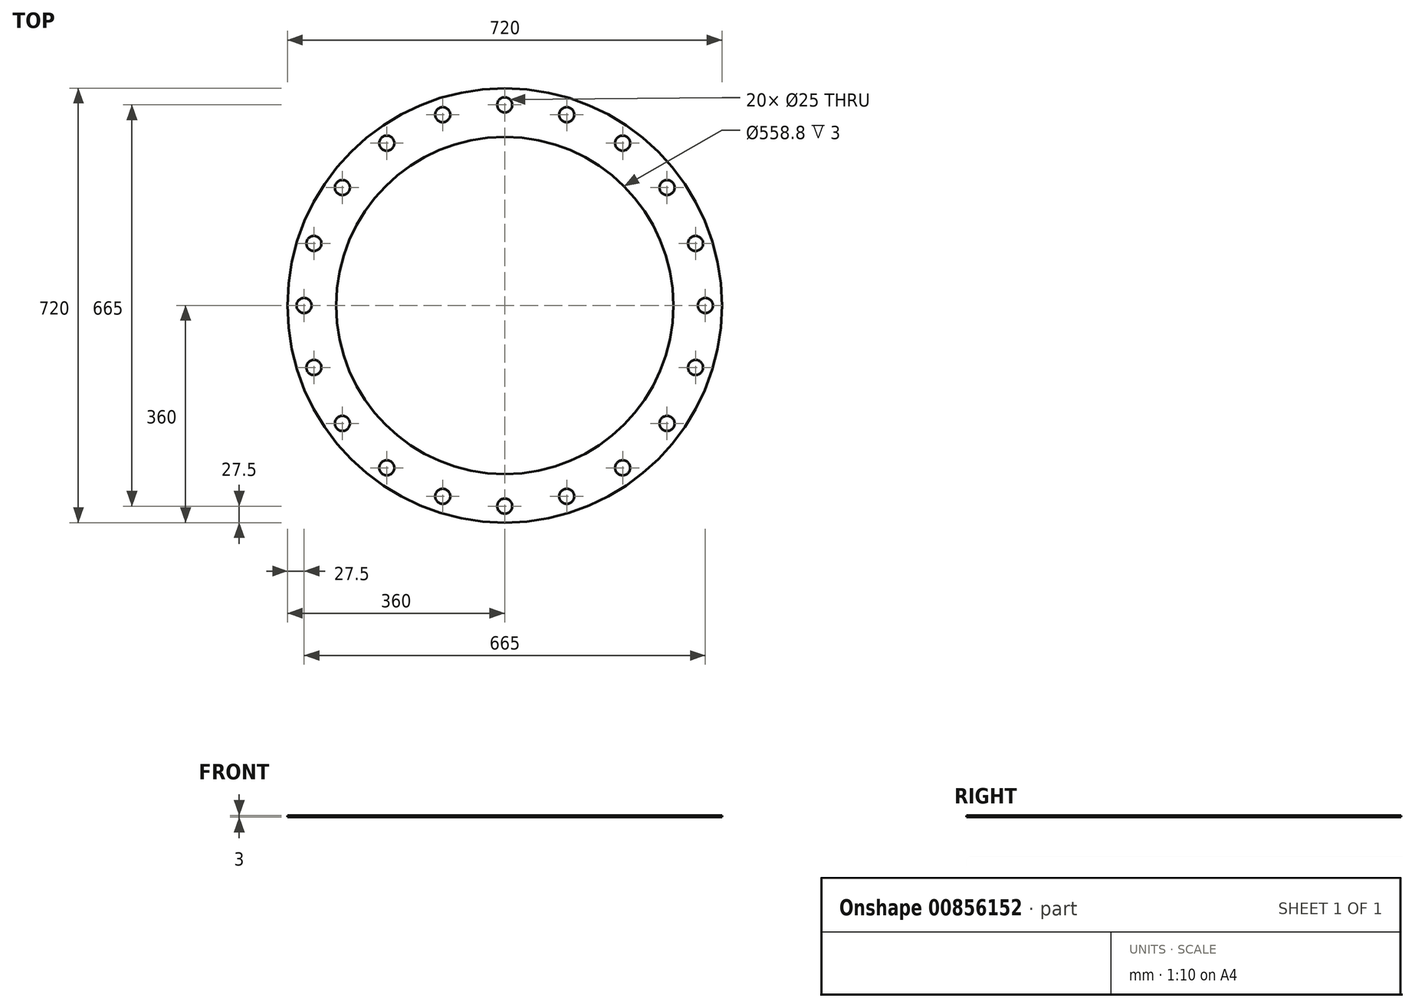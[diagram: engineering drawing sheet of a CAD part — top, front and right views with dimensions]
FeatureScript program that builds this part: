
annotation { "Feature Type Name" : "Feature", "Feature Type Description" : "" }
export const myFeature = defineFeature(function(context is Context, id is Id, definition is map)
    precondition{}
    {
        {
            var Q0;
            Q0=qCreatedBy(makeId("Top.planeOp"),FACE);
            var sketch = newSketch(context, id + "F0", { "sketchPlane" : qUnion([Q0])});
            skCircle(sketch, "E0", {"center": v(0, 0) * mm, "radius": 360 * mm});
            skLineSegment(sketch, "E1", {"start": v(423.48, 0) * mm, "end": v(-426.4, 0) * mm, "construction": true});
            skLineSegment(sketch, "E2", {"start": v(0, 375.02) * mm, "end": v(0, -391.8) * mm, "construction": true});
            skCircle(sketch, "E3", {"center": v(102.75, 316.23) * mm, "radius": 12.5 * mm});
            skCircle(sketch, "E4.1.0", {"center": v(0, 332.5) * mm, "radius": 12.5 * mm});
            skCircle(sketch, "E4.2.0", {"center": v(-102.75, 316.23) * mm, "radius": 12.5 * mm});
            skCircle(sketch, "E4.3.0", {"center": v(-195.44, 269) * mm, "radius": 12.5 * mm});
            skCircle(sketch, "E4.4.0", {"center": v(-269, 195.44) * mm, "radius": 12.5 * mm});
            skCircle(sketch, "E4.5.0", {"center": v(-316.23, 102.75) * mm, "radius": 12.5 * mm});
            skCircle(sketch, "E4.6.0", {"center": v(-332.5, 0) * mm, "radius": 12.5 * mm});
            skCircle(sketch, "E4.7.0", {"center": v(-316.23, -102.75) * mm, "radius": 12.5 * mm});
            skCircle(sketch, "E4.8.0", {"center": v(-269, -195.44) * mm, "radius": 12.5 * mm});
            skCircle(sketch, "E4.9.0", {"center": v(-195.44, -269) * mm, "radius": 12.5 * mm});
            skCircle(sketch, "E4.10.0", {"center": v(-102.75, -316.23) * mm, "radius": 12.5 * mm});
            skCircle(sketch, "E4.11.0", {"center": v(0, -332.5) * mm, "radius": 12.5 * mm});
            skCircle(sketch, "E4.12.0", {"center": v(102.75, -316.23) * mm, "radius": 12.5 * mm});
            skCircle(sketch, "E4.13.0", {"center": v(195.44, -269) * mm, "radius": 12.5 * mm});
            skCircle(sketch, "E4.14.0", {"center": v(269, -195.44) * mm, "radius": 12.5 * mm});
            skCircle(sketch, "E4.15.0", {"center": v(316.23, -102.75) * mm, "radius": 12.5 * mm});
            skCircle(sketch, "E4.16.0", {"center": v(332.5, 0) * mm, "radius": 12.5 * mm});
            skCircle(sketch, "E4.17.0", {"center": v(316.23, 102.75) * mm, "radius": 12.5 * mm});
            skCircle(sketch, "E4.18.0", {"center": v(269, 195.44) * mm, "radius": 12.5 * mm});
            skCircle(sketch, "E4.19.0", {"center": v(195.44, 269) * mm, "radius": 12.5 * mm});
            skCircle(sketch, "E5", {"center": v(0, 0) * mm, "radius": 279.4 * mm});
            skCircle(sketch, "E6", {"center": v(0, 0) * mm, "radius": 332.5 * mm, "construction": true});
            skSolve(sketch);
        }
        {
            var Q0;
            Q0=makeQuery(id+"F0.imprint","IMPRINT",FACE,{"disambiguationData":[TD([[makeQuery(id+"F0.imprint","IMPRINT",EDGE,{"derivedFrom":sQuery(id+"F0.wireOp",EDGE,"E0")}),1.0]])]});
            extrude(context, id + "F1", {"entities" : qUnion([Q0]), "depth" : 3 * mm, "offsetDistance" : 25 * mm});
        }
    });
